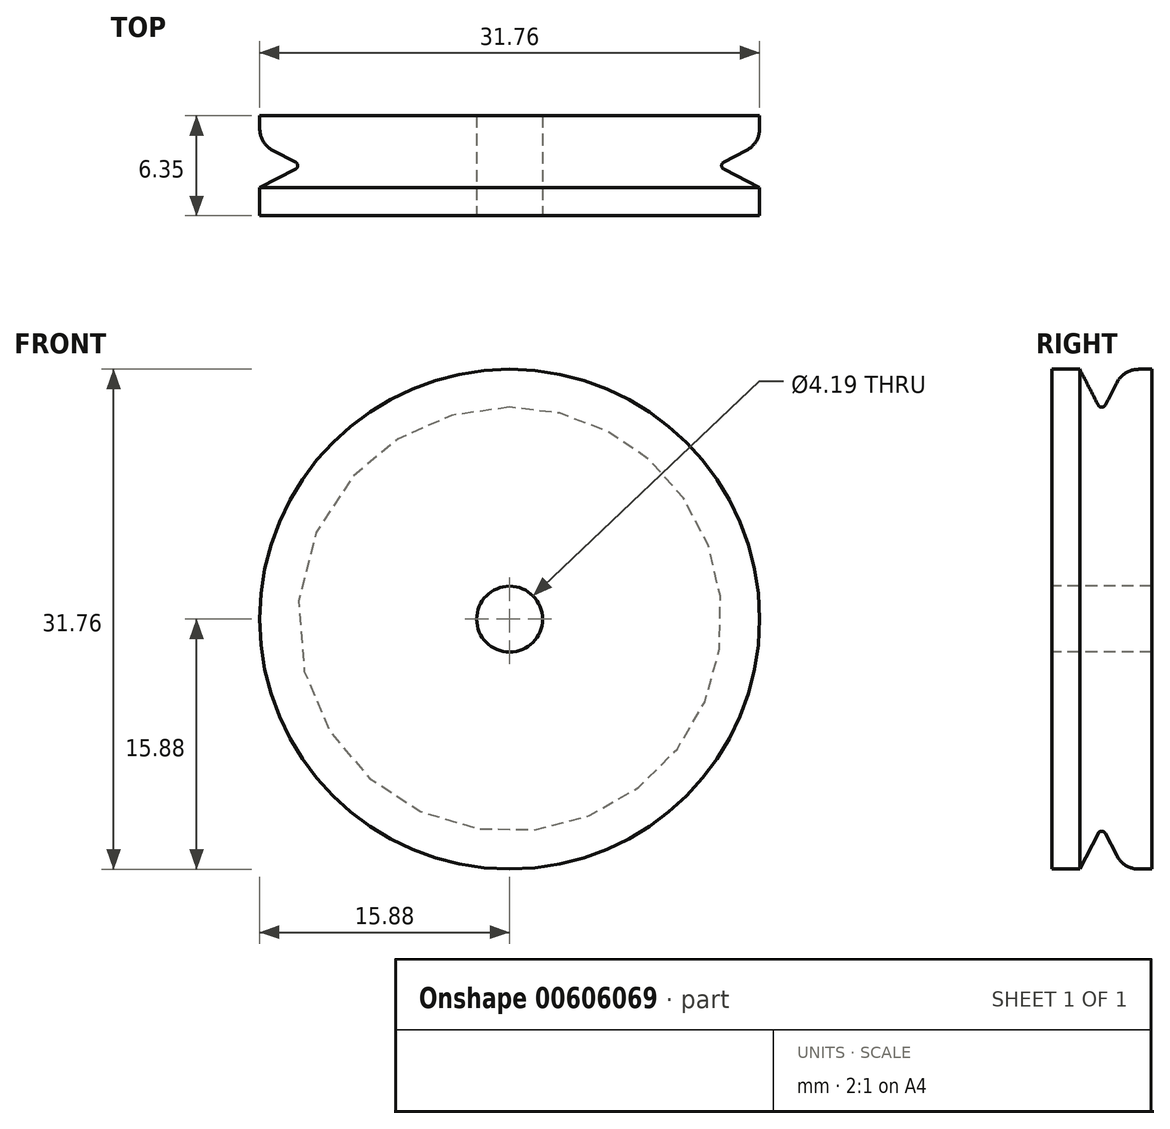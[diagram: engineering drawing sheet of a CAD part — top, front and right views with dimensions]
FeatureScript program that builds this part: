
annotation { "Feature Type Name" : "Feature", "Feature Type Description" : "" }
export const myFeature = defineFeature(function(context is Context, id is Id, definition is map)
    precondition{}
    {
        {
            var Q0;
            Q0=qCreatedBy(makeId("Front.planeOp"),FACE);
            var sketch = newSketch(context, id + "F0", { "sketchPlane" : qUnion([Q0])});
            skCircle(sketch, "E0", {"center": v(0, 0) * mm, "radius": 15.88 * mm});
            skSolve(sketch);
        }
        {
            var Q0;
            Q0=makeQuery(id+"F0.imprint","IMPRINT",FACE,{"disambiguationData":[TD([[makeQuery(id+"F0.imprint","IMPRINT",EDGE,{"derivedFrom":sQuery(id+"F0.wireOp",EDGE,"E0")}),1.0]])]});
            extrude(context, id + "F1", {"entities" : qUnion([Q0]), "depth" : 6.35 * mm, "offsetDistance" : 25.4 * mm});
        }
        {
            var Q0;
            Q0=makeQuery(id+"F1.opExtrude","CAP_FACE",FACE,{"disambiguationData":[OSD([sQuery(id+"F0.wireOp",EDGE,"E0")])],"isStart":false});
            var sketch = newSketch(context, id + "F2", { "sketchPlane" : qUnion([Q0])});
            skCircle(sketch, "E1", {"center": v(0, 0) * mm, "radius": 2.1 * mm});
            skSolve(sketch);
        }
        {
            var Q0;
            Q0=makeQuery(id+"F2.imprint","IMPRINT",FACE,{"disambiguationData":[TD([[makeQuery(id+"F2.imprint","IMPRINT",EDGE,{"derivedFrom":sQuery(id+"F2.wireOp",EDGE,"E1")}),1.0]])]});
            extrude(context, id + "F3", {"entities" : qUnion([Q0]), "operationType" : NewBodyOperationType.REMOVE, "oppositeDirection" : true, "depth" : 6.35 * mm, "offsetDistance" : 25.4 * mm});
        }
        {
            var Q0;
            Q0=qCreatedBy(makeId("Right.planeOp"),FACE);
            var sketch = newSketch(context, id + "F4", { "sketchPlane" : qUnion([Q0])});
            skLineSegment(sketch, "E2.0", {"start": v(-6.35, -15.88) * mm, "end": v(-6.35, 15.88) * mm});
            skLineSegment(sketch, "E3", {"start": v(-6.35, 2.1) * mm, "end": v(0, 2.1) * mm});
            skLineSegment(sketch, "E4", {"start": v(-4.57, 15.88) * mm, "end": v(-3.4, 13.6) * mm});
            skLineSegment(sketch, "E5", {"start": v(-2.95, 13.6) * mm, "end": v(-1.78, 15.88) * mm});
            skLineSegment(sketch, "E6", {"start": v(-1.78, 15.88) * mm, "end": v(-4.57, 15.88) * mm});
            skPoint(sketch, "E7.visualSharp", {"position": v(-3.18, 13.17) * mm});
            skArc(sketch, "E7.filletArc", {"start": v(-3.4, 13.6) * mm, "mid": v(-3.17, 13.46) * mm, "end": v(-2.95, 13.6) * mm});
            skLineSegment(sketch, "E8", {"start": v(-4.57, 15.88) * mm, "end": v(-1.78, 15.88) * mm});
            skSolve(sketch);
        }
        {
            var Q0;
            Q0=qCreatedBy(makeId("Top.planeOp"),FACE);
            var sketch = newSketch(context, id + "F5", { "sketchPlane" : qUnion([Q0])});
            skLineSegment(sketch, "E9", {"start": v(0, 0) * mm, "end": v(0, -6.35) * mm});
            skSolve(sketch);
        }
        {
            var Q0;
            Q0 = qSketchRegion(id + "F4", true);
            var Q1;
            Q1=sQuery(id+"F5.wireOp",EDGE,"E9");
            revolve(context, id + "F6", {"operationType" : NewBodyOperationType.REMOVE, "entities" : qUnion([Q0]), "axis" : qUnion([Q1]), "revolveType" : RevolveType.FULL});
        }
        {
            var Q0;
            Q0=makeQuery(id+"F6.boolean.opBoolean","COPY",EDGE,{"derivedFrom":makeQuery(id+"F6.opRevolve","SWEPT_EDGE",EDGE,{"disambiguationData":[OSD([sQuery(id+"F4.wireOp",EDGE,"E4"),sQuery(id+"F4.wireOp",EDGE,"E8")])]})});
            var Q1;
            Q1=makeQuery(id+"F6.boolean.opBoolean","COPY",EDGE,{"derivedFrom":makeQuery(id+"F6.opRevolve","SWEPT_EDGE",EDGE,{"disambiguationData":[OSD([sQuery(id+"F4.wireOp",EDGE,"E5"),sQuery(id+"F4.wireOp",EDGE,"E8")])]})});
            fillet(context, id + "F7", {"entities" : qUnion([Q0, Q1]), "radius" : 1.59 * mm, "tangentPropagation" : true, "allowEdgeOverflow" : false});
        }
    });
